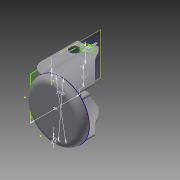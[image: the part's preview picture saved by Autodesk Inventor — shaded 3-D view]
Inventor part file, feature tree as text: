
AUTODESK INVENTOR PART (.ipt)
format: ipt  version: 2014 (Build 180170000, 170)  size: 282,112 bytes
history: native  units: mm
features: sketch x10, fillet x10, extrude x7, plane x5, chamfer x4, shell x1, hole x1
ambient origin geometry x8: Origin, YZ Plane, XZ Plane, XY Plane, X Axis, Y Axis, Z Axis, Center Point
bodies: Solid1 (feature_tree)
feature tree (38):
  extrude  "Extrusion1"  Depth=1.0mm TaperAngle=0.0deg
  shell  "Shell1"  Thickness=1.0mm
  sketch  "Sketch2"  dims[d4=29.0mm d5=30.0mm d8=26.0mm]
  plane  "Work Plane1"
  sketch  "Sketch4"  dims[d9=10.0mm d10=10.0mm]
  extrude  "Extrusion4"  Depth=30.0mm
  fillet  "Fillet1"  Radius=26.0mm
  extrude  "Extrusion5"  Depth=10.0mm
  chamfer  "Chamfer1"  Distance=25.0mm
  chamfer  "Chamfer2"  Distance=18.0mm
  chamfer  "Chamfer3"  Distance=9.0mm Angle=45.0deg
  fillet  "Fillet2"  Radius=9.0mm
  chamfer  "Chamfer4"  Distance=5.0mm Angle=45.0deg
  fillet  "Fillet3"  Radius=9.0mm
  fillet  "Fillet4"  Radius=4.0mm
  fillet  "Fillet5"  Radius=4.0mm
  fillet  "Fillet6"  Radius=15.0mm
  fillet  "Fillet7"  Radius=15.0mm
  plane  "Work Plane3"
  sketch  "Sketch6"  dims[d11=0.5mm]
  plane  "Work Plane4"
  sketch  "Sketch7"  dims[d12=0.5mm d15=25.0mm d16=0.0mm]
  plane  "Work Plane5"
  extrude  "Extrusion7"  Depth=5.0mm
  plane  "Work Plane6"
  extrude  "Extrusion8"  Depth=1.0mm
  extrude  "Extrusion9"  Depth=1.0mm TaperAngle=0.0deg
  extrude  "Extrusion10"  Depth=1.0mm
  fillet  "Fillet11"  Radius=6.0mm
  fillet  "Fillet12"  Radius=25.0mm
  fillet  "Fillet13"  Radius=6.0mm
  hole  "Hole3"  [1 undecoded]
  sketch  "Sketch1"  dims[d0=30.0mm d1=4.0mm d2=0.0mm d3=1.0mm]
  sketch  "Sketch9"  dims[d17=3.0mm d19=18.0mm d20=0.0mm d21=9.0mm d22=2.0mm d23=45.0deg]
  sketch  "Sketch10"  dims[d24=9.0mm d25=2.0mm d26=45.0deg]
  sketch  "Sketch11"  dims[d27=5.0mm d28=2.0mm d29=45.0deg d30=9.0mm d31=5.0mm d32=2.0mm d33=45.0deg d34=9.0mm d35=4.0mm d36=4.0mm d37=15.0mm d38=15.0mm]
  sketch  "Sketch12"  dims[d51=5.0mm d52=5.0mm]
  sketch  "Sketch13"  dims[d66=25.0mm d67=25.0mm d68=1.0mm d69=0.0mm d71=25.0mm d72=6.0mm d73=25.0mm d74=6.0mm d75=1.0mm d76=0.0mm d78=25.0mm d79=1.0mm d80=25.0mm d81=0.75mm d82=0.0mm d83=1.0mm d84=25.0mm d85=1.0mm d86=0.75mm d87=0.0mm d88=2.0mm d89=1.0mm d90=6.0mm d91=5.0mm d92=3.5mm d93=5.0mm d94=5.0mm d95=6.0mm d96=4.0mm d97=2.0mm d98=90.0deg d99=8.0mm d100=20.594885mm d44=1.0mm d45=1.0mm]
note: 1 required parameter value undecoded (feature->parameter linkage not recoverable at this tier; creation-order binding heuristic only, values carry confidence <= 0.55)
